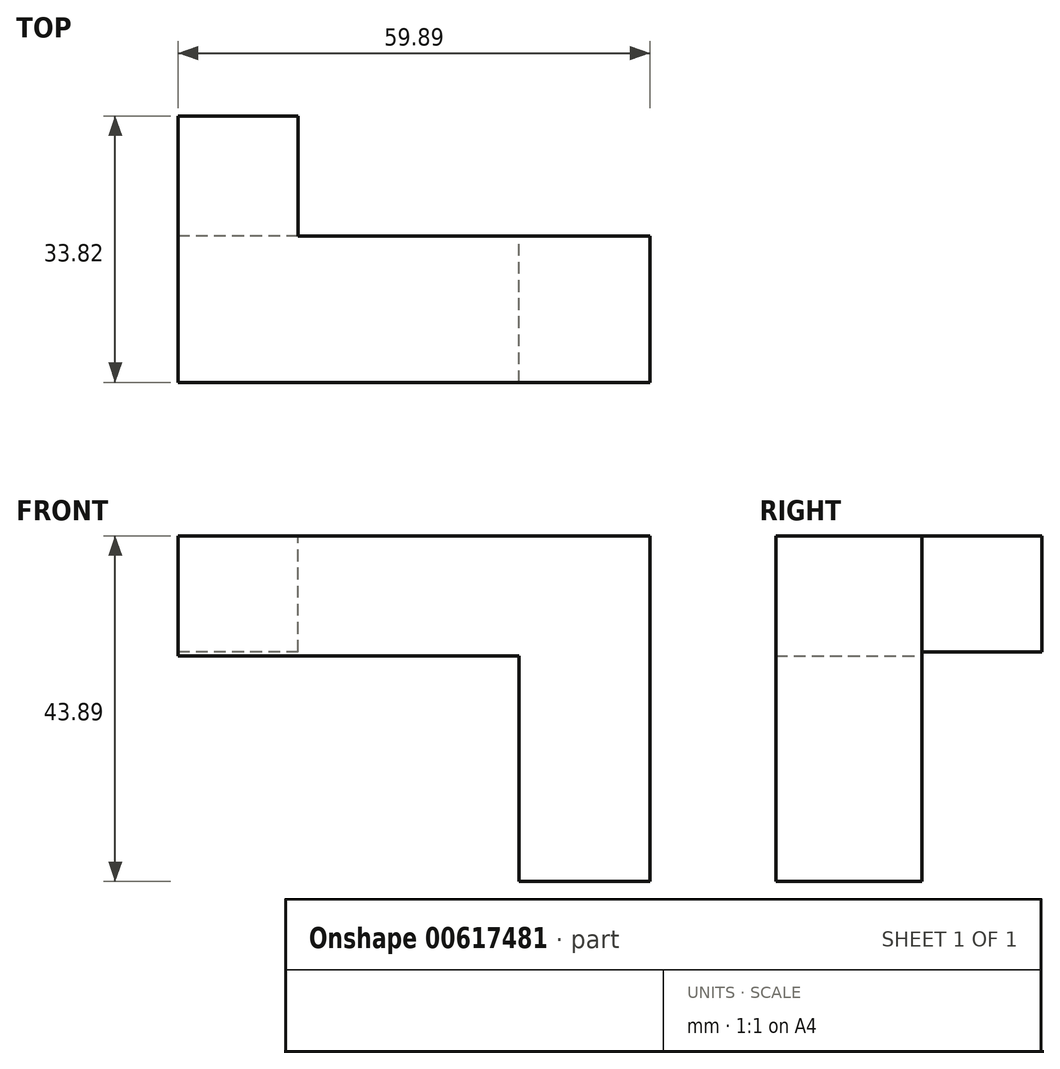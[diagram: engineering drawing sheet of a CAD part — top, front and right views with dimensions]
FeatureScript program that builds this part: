
annotation { "Feature Type Name" : "Feature", "Feature Type Description" : "" }
export const myFeature = defineFeature(function(context is Context, id is Id, definition is map)
    precondition{}
    {
        {
            var Q0;
            Q0=qCreatedBy(makeId("Front.planeOp"),FACE);
            var sketch = newSketch(context, id + "F0", { "sketchPlane" : qUnion([Q0])});
            skLineSegment(sketch, "E0", {"start": v(0, 0) * mm, "end": v(-59.9, 0) * mm});
            skLineSegment(sketch, "E1", {"start": v(-59.9, 0) * mm, "end": v(-59.9, -15.24) * mm});
            skLineSegment(sketch, "E2", {"start": v(-59.9, -15.24) * mm, "end": v(-16.61, -15.24) * mm});
            skLineSegment(sketch, "E3", {"start": v(-16.61, -15.24) * mm, "end": v(-16.61, -43.9) * mm});
            skLineSegment(sketch, "E4", {"start": v(-16.61, -43.9) * mm, "end": v(0, -43.9) * mm});
            skLineSegment(sketch, "E5", {"start": v(0, 0) * mm, "end": v(0, -43.9) * mm});
            skLineSegment(sketch, "E6", {"start": v(-59.9, -15.24) * mm, "end": v(-44.65, -15.24) * mm});
            skLineSegment(sketch, "E7", {"start": v(-44.65, -15.24) * mm, "end": v(-44.65, 0) * mm});
            skLineSegment(sketch, "E8", {"start": v(-44.65, 0) * mm, "end": v(-59.9, 0) * mm});
            skSolve(sketch);
        }
        {
            var Q0;
            Q0 = qSketchRegion(id + "F0", true);
            extrude(context, id + "F1", {"entities" : qUnion([Q0]), "depth" : 18.58 * mm, "offsetDistance" : 25.4 * mm});
        }
        {
            var Q0;
            Q0=qCreatedBy(makeId("Top.planeOp"),FACE);
            var sketch = newSketch(context, id + "F2", { "sketchPlane" : qUnion([Q0])});
            skLineSegment(sketch, "E9", {"start": v(0, 0) * mm, "end": v(-59.9, 0) * mm});
            skLineSegment(sketch, "E10", {"start": v(-59.9, 0) * mm, "end": v(-59.9, 15.24) * mm});
            skLineSegment(sketch, "E11", {"start": v(-59.9, 15.24) * mm, "end": v(-44.65, 15.24) * mm});
            skLineSegment(sketch, "E12", {"start": v(-44.65, 15.24) * mm, "end": v(-44.65, 0) * mm});
            skSolve(sketch);
        }
        {
            var Q0;
            Q0 = qSketchRegion(id + "F2", true);
            extrude(context, id + "F3", {"entities" : qUnion([Q0]), "operationType" : NewBodyOperationType.ADD, "oppositeDirection" : true, "depth" : 14.73 * mm, "offsetDistance" : 25.4 * mm});
        }
    });
